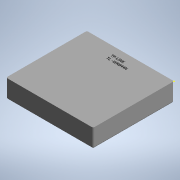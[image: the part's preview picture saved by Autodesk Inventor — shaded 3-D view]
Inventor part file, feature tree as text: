
AUTODESK INVENTOR PART (.ipt)
format: ipt  version: 2022 (Build 260153000, 153)  size: 135,168 bytes
history: native  units: mm (DEFAULTED — no unit token found)
features: other x8, sketch x3, extrude x2, fillet x1, projected_geometry x1
bodies: Body1 (feature_tree)
feature tree (15):
  other  "Sólido1"
  other  "Origen"
  extrude  "Extrusión1"  Depth=106.7mm
  fillet  "Empalme1"  Radius=24.3mm
  extrude  "Extrusión2"  Depth=2.0mm
  sketch  "Boceto4"  dims[d7=40.0mm d9=10.37mm d11=7.0mm d13=7.0mm d15=4.87mm d17=4.87mm d18=7.0mm d19=7.0mm d20=4.87mm d21=4.87mm d22=21.0mm d23=0.0mm]
  other  "Plano YZ"
  other  "Plano XZ"
  other  "Plano XY"
  other  "Eje X"
  other  "Eje Y"
  other  "Eje Z"
  sketch  "Boceto1"  dims[d0=115.0mm d1=106.7mm d2=24.3mm d3=0.0mm]
  sketch  "Boceto2"  dims[d4=2.0mm d5=111.0mm]
  projected_geometry  "Contorno proyectado1"
